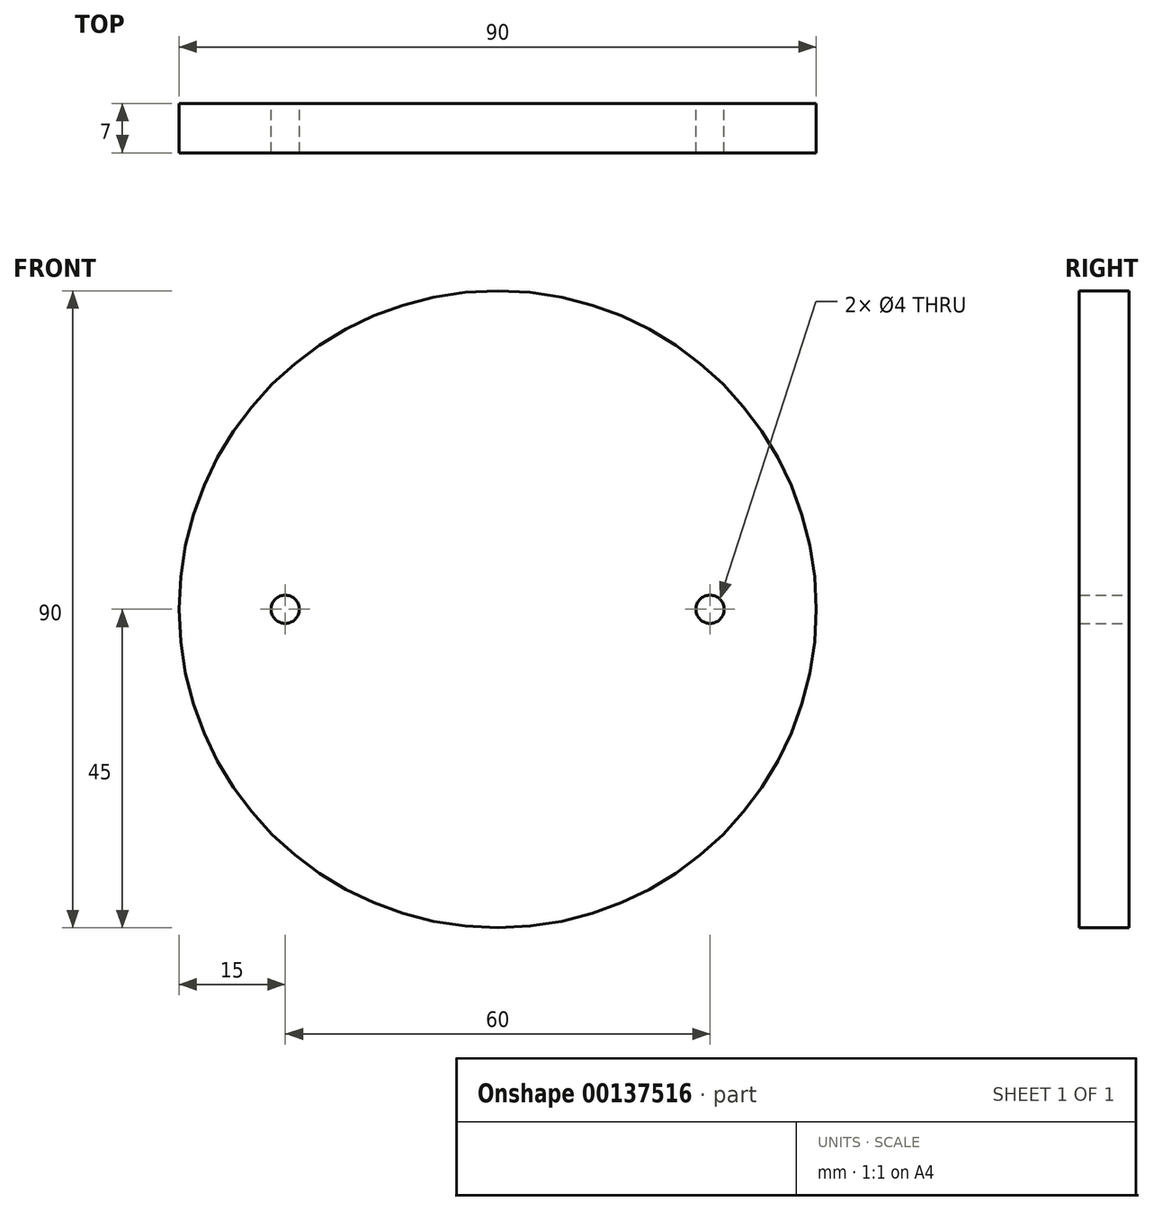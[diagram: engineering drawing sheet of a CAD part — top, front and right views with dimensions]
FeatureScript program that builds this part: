
annotation { "Feature Type Name" : "Feature", "Feature Type Description" : "" }
export const myFeature = defineFeature(function(context is Context, id is Id, definition is map)
    precondition{}
    {
        {
            var Q0;
            Q0=qCreatedBy(makeId("Front.planeOp"),FACE);
            var sketch = newSketch(context, id + "F0", { "sketchPlane" : qUnion([Q0])});
            skCircle(sketch, "E0", {"center": v(0, 0) * mm, "radius": 45 * mm});
            skLineSegment(sketch, "E1", {"start": v(-28, 0) * mm, "end": v(-30, 0) * mm});
            skCircle(sketch, "E2", {"center": v(-30, 0) * mm, "radius": 2 * mm});
            skCircle(sketch, "E3", {"center": v(30, 0) * mm, "radius": 2 * mm});
            skLineSegment(sketch, "E4.trimOffspring", {"start": v(28, 0) * mm, "end": v(30, 0) * mm});
            skLineSegment(sketch, "E5", {"start": v(-45, 0) * mm, "end": v(45, 0) * mm});
            skSolve(sketch);
        }
        {
            var Q0;
            {var subQ0=sQuery(id+"F0.wireOp",EDGE,"E5");var subQ1=sQuery(id+"F0.wireOp",EDGE,"E0");var subQ2=makeQuery(id+"F0.imprint","INTERSECT",VERTEX,{"disambiguationData":[OD(0.0)],"derivedFrom":[subQ1,subQ0]});Q0=makeQuery(id+"F0.imprint","IMPRINT",FACE,{"disambiguationData":[TD([[makeQuery(id+"F0.imprint","IMPRINT",EDGE,{"disambiguationData":[TD([[subQ2,1.0]])],"derivedFrom":subQ1}),1.0]])]});}
            var Q1;
            {var subQ0=sQuery(id+"F0.wireOp",EDGE,"E5");var subQ1=sQuery(id+"F0.wireOp",EDGE,"E0");var subQ2=makeQuery(id+"F0.imprint","INTERSECT",VERTEX,{"disambiguationData":[OD(0.0)],"derivedFrom":[subQ1,subQ0]});Q1=makeQuery(id+"F0.imprint","IMPRINT",FACE,{"disambiguationData":[TD([[makeQuery(id+"F0.imprint","IMPRINT",EDGE,{"disambiguationData":[TD([[subQ2,-1.0]])],"derivedFrom":subQ1}),1.0]])]});}
            extrude(context, id + "F1", {"entities" : qUnion([Q0, Q1]), "depth" : 7 * mm, "symmetric" : true});
        }
    });
